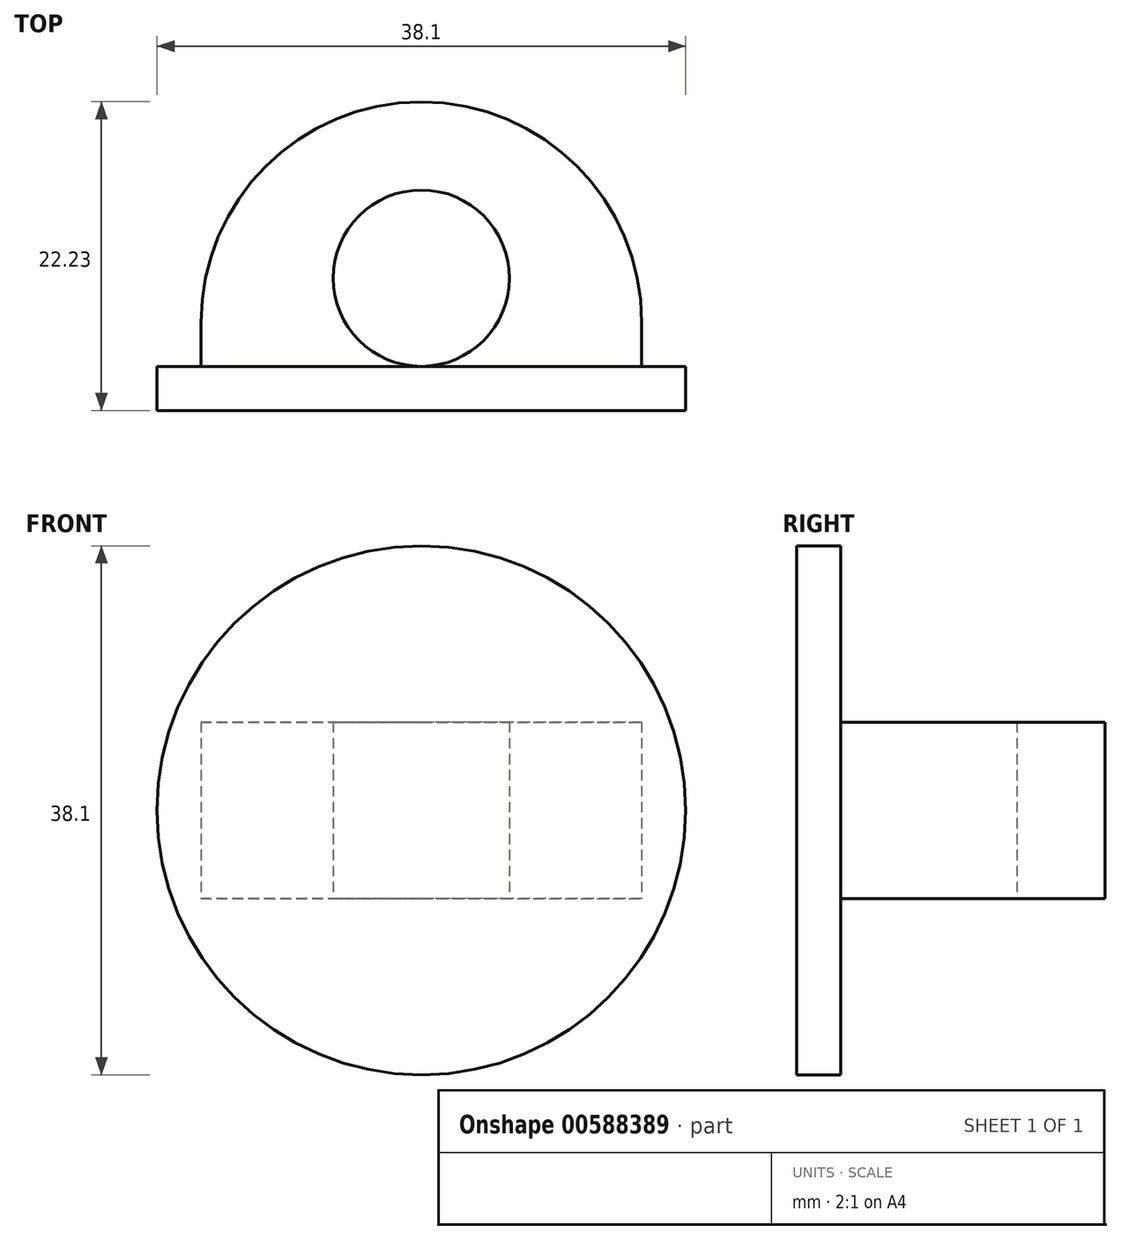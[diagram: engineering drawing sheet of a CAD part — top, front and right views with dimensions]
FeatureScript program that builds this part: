
annotation { "Feature Type Name" : "Feature", "Feature Type Description" : "" }
export const myFeature = defineFeature(function(context is Context, id is Id, definition is map)
    precondition{}
    {
        {
            var Q0;
            Q0=qCreatedBy(makeId("Front.planeOp"),FACE);
            var sketch = newSketch(context, id + "F0", { "sketchPlane" : qUnion([Q0])});
            skCircle(sketch, "E0", {"center": v(0, 0) * mm, "radius": 19.05 * mm});
            skCircle(sketch, "E1", {"center": v(0, 0) * mm, "radius": 9.53 * mm});
            skSolve(sketch);
        }
        {
            var Q0;
            Q0=qCreatedBy(makeId("Top.planeOp"),FACE);
            var sketch = newSketch(context, id + "F1", { "sketchPlane" : qUnion([Q0])});
            skLineSegment(sketch, "E2", {"start": v(0, 0) * mm, "end": v(0, 6.35) * mm, "construction": true});
            skArc(sketch, "E3", {"start": v(-15.88, 6.35) * mm, "mid": v(0, 22.22) * mm, "end": v(15.88, 6.35) * mm});
            skLineSegment(sketch, "E4", {"start": v(-15.88, 6.35) * mm, "end": v(-15.88, 0) * mm});
            skLineSegment(sketch, "E5", {"start": v(15.88, 6.35) * mm, "end": v(15.88, 0) * mm});
            skLineSegment(sketch, "E6", {"start": v(15.88, 0) * mm, "end": v(-15.88, 0) * mm});
            skLineSegment(sketch, "E7", {"start": v(0, 0) * mm, "end": v(0, 9.53) * mm, "construction": true});
            skCircle(sketch, "E8", {"center": v(0, 9.53) * mm, "radius": 6.35 * mm});
            skSolve(sketch);
        }
        {
            var Q0;
            Q0 = qSketchRegion(id + "F1", true);
            extrude(context, id + "F2", {"entities" : qUnion([Q0]), "endBound" : BoundingType.SYMMETRIC, "depth" : 12.7 * mm, "offsetDistance" : 25.4 * mm});
        }
        {
            var Q0;
            Q0=makeQuery(id+"F0.imprint","IMPRINT",FACE,{"disambiguationData":[TD([[makeQuery(id+"F0.imprint","IMPRINT",EDGE,{"derivedFrom":sQuery(id+"F0.wireOp",EDGE,"E0")}),1.0]])]});
            var Q1;
            Q1=makeQuery(id+"F0.imprint","IMPRINT",FACE,{"disambiguationData":[TD([[makeQuery(id+"F0.imprint","IMPRINT",EDGE,{"derivedFrom":sQuery(id+"F0.wireOp",EDGE,"E1")}),1.0]])]});
            var Q2;
            Q2=sQuery(id+"F0.wireOp",EDGE,"E0");
            extrude(context, id + "F3", {"entities" : qUnion([Q0, Q1]), "operationType" : NewBodyOperationType.ADD, "surfaceEntities" : qUnion([Q2]), "depth" : -3.17 * mm, "offsetDistance" : 25.4 * mm});
        }
    });
